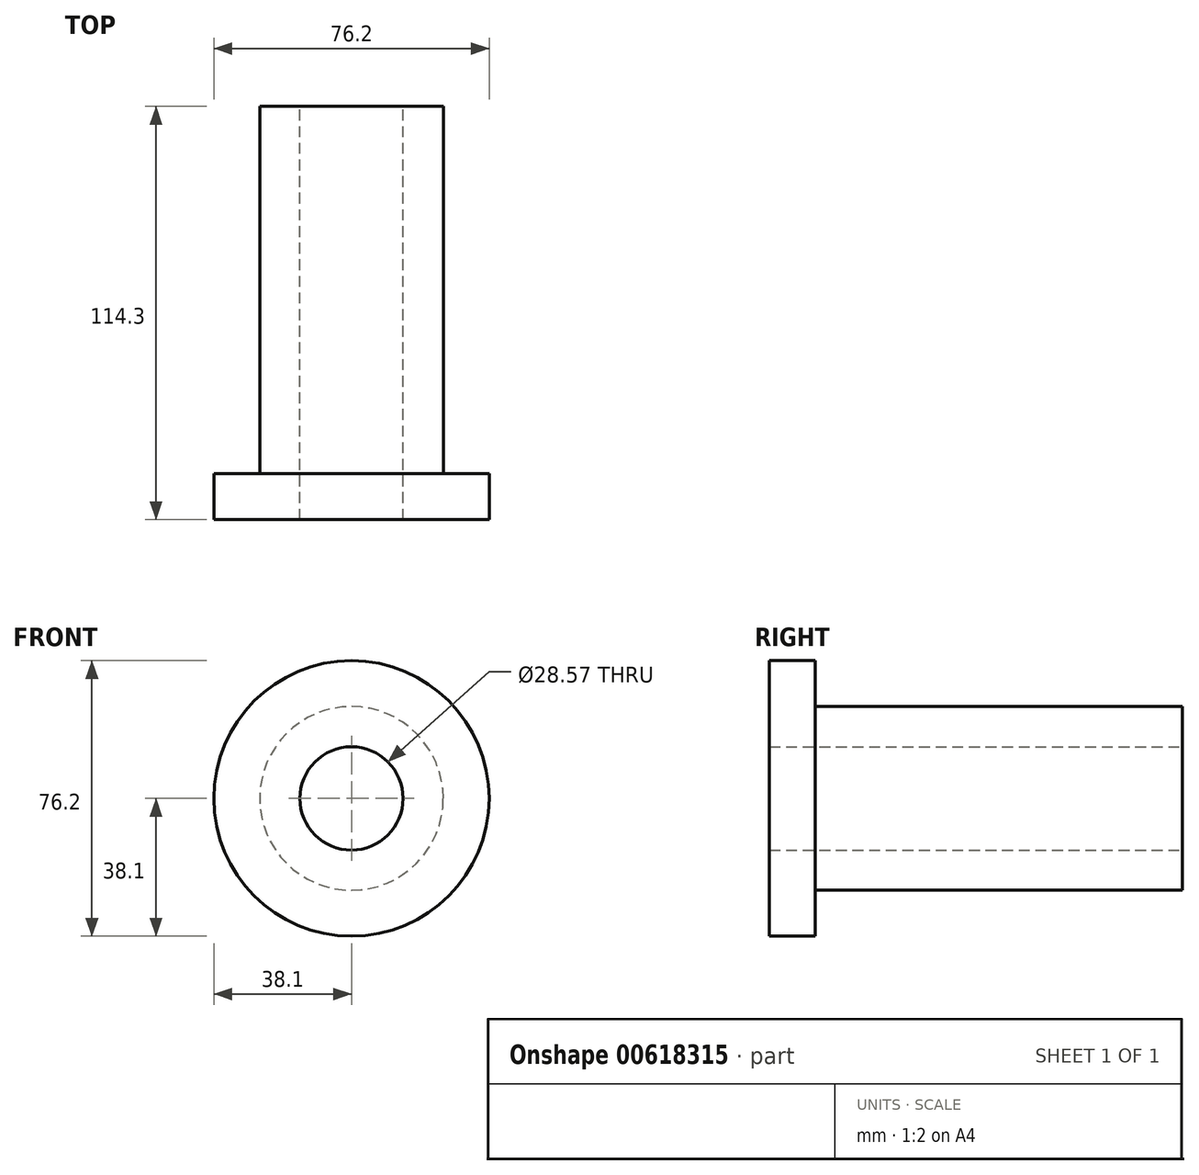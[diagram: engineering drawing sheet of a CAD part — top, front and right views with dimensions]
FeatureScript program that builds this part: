
annotation { "Feature Type Name" : "Feature", "Feature Type Description" : "" }
export const myFeature = defineFeature(function(context is Context, id is Id, definition is map)
    precondition{}
    {
        {
            var Q0;
            Q0=qCreatedBy(makeId("Front.planeOp"),FACE);
            var sketch = newSketch(context, id + "F0", { "sketchPlane" : qUnion([Q0])});
            skCircle(sketch, "E0", {"center": v(0, 0) * mm, "radius": 25.4 * mm});
            skCircle(sketch, "E1", {"center": v(0, 0) * mm, "radius": 14.29 * mm});
            skSolve(sketch);
        }
        {
            var Q0;
            Q0=qSketchRegion(id+"F0",true);
            extrude(context, id + "F1", {"entities" : qUnion([Q0]), "depth" : 114.3 * mm, "offsetDistance" : 25.4 * mm});
        }
        {
            var Q0;
            Q0=makeQuery(id+"F1.opExtrude","CAP_FACE",FACE,{"disambiguationData":[OSD([sQuery(id+"F0.wireOp",EDGE,"E0"),sQuery(id+"F0.wireOp",EDGE,"E1")])],"isStart":false});
            var sketch = newSketch(context, id + "F2", { "sketchPlane" : qUnion([Q0])});
            skCircle(sketch, "E2.0", {"center": v(0, 0) * mm, "radius": 38.1 * mm});
            skSolve(sketch);
        }
        {
            var Q0;
            Q0=makeQuery(id+"F2.imprint","IMPRINT",FACE,{"disambiguationData":[TD([[makeQuery(id+"F2.imprint","IMPRINT",EDGE,{"derivedFrom":sQuery(id+"F2.wireOp",EDGE,"E2.0")}),1.0]])]});
            extrude(context, id + "F3", {"entities" : qUnion([Q0]), "operationType" : NewBodyOperationType.ADD, "oppositeDirection" : true, "depth" : 12.7 * mm, "offsetDistance" : 25.4 * mm});
        }
    });
